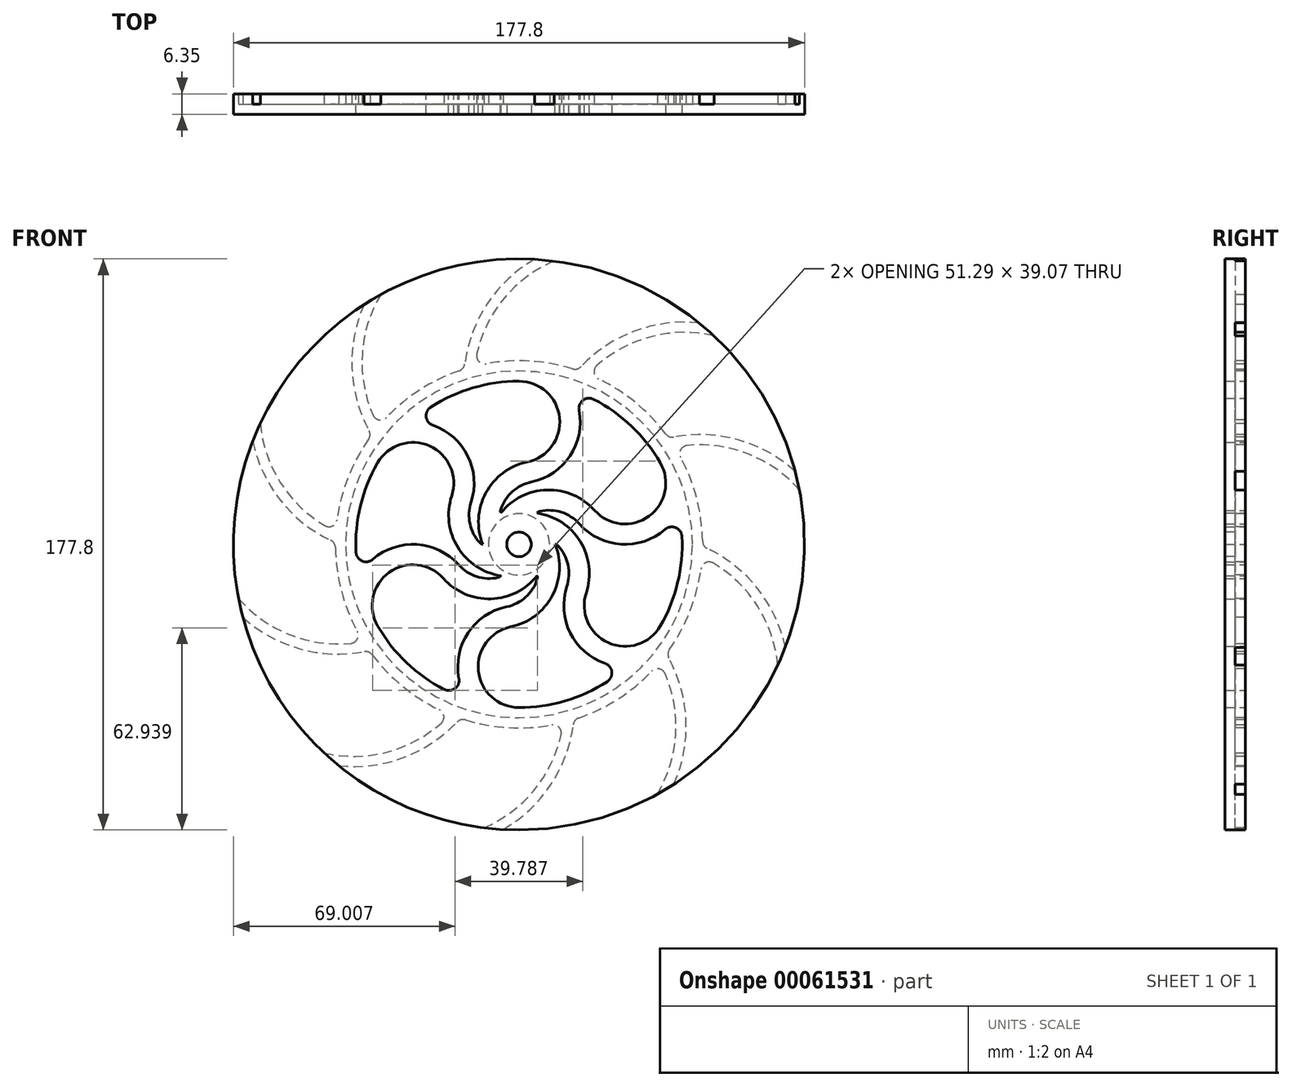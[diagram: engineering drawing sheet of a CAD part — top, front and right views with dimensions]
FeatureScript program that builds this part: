
annotation { "Feature Type Name" : "Feature", "Feature Type Description" : "" }
export const myFeature = defineFeature(function(context is Context, id is Id, definition is map)
    precondition{}
    {
        {
            var Q0;
            Q0=qCreatedBy(makeId("Front.planeOp"),FACE);
            var sketch = newSketch(context, id + "F0", { "sketchPlane" : qUnion([Q0])});
            skCircle(sketch, "E0", {"center": v(0, 0) * mm, "radius": 88.9 * mm});
            skSolve(sketch);
        }
        {
            var Q0;
            Q0=makeQuery(id+"F0.imprint","IMPRINT",FACE,{"disambiguationData":[TD([[makeQuery(id+"F0.imprint","IMPRINT",EDGE,{"derivedFrom":sQuery(id+"F0.wireOp",EDGE,"E0")}),1.0]])]});
            extrude(context, id + "F1", {"entities" : qUnion([Q0]), "depth" : 6.35 * mm});
        }
        {
            var Q0;
            Q0=makeQuery(id+"F1.opExtrude","CAP_FACE",FACE,{"disambiguationData":[OSD([sQuery(id+"F0.wireOp",EDGE,"E0")])],"isStart":false});
            var sketch = newSketch(context, id + "F2", { "sketchPlane" : qUnion([Q0])});
            skCircle(sketch, "E1", {"center": v(0, 0) * mm, "radius": 57.15 * mm});
            skCircle(sketch, "E2", {"center": v(0, 0) * mm, "radius": 53.98 * mm});
            skSolve(sketch);
        }
        {
            var Q0;
            Q0=qSketchRegion(id+"F2",true);
            extrude(context, id + "F3", {"entities" : qUnion([Q0]), "operationType" : NewBodyOperationType.ADD, "depth" : 41.27 * mm});
        }
        {
            var Q0;
            {var subQ0=sQuery(id+"F0.wireOp",EDGE,"E0");Q0=makeQuery(id+"F3.boolean.opBoolean","SPLIT",FACE,{"disambiguationData":[TD([makeQuery(id+"F1.opExtrude","SWEPT_FACE",FACE,{"disambiguationData":[OSD([subQ0])]})])],"derivedFrom":makeQuery(id+"F1.opExtrude","CAP_FACE",FACE,{"disambiguationData":[OSD([subQ0])],"isStart":false})});}
            var sketch = newSketch(context, id + "F4", { "sketchPlane" : qUnion([Q0])});
            skArc(sketch, "E3", {"start": v(80.54, -37.63) * mm, "mid": v(72.26, -16.34) * mm, "end": v(53.9, -2.7) * mm});
            skArc(sketch, "E4", {"start": v(82.9, -32.09) * mm, "mid": v(72.74, -11.92) * mm, "end": v(53.97, 0.64) * mm});
            skArc(sketch, "E5.0", {"start": v(53.9, -2.7) * mm, "mid": v(53.97, -1.03) * mm, "end": v(53.97, 0.64) * mm});
            skArc(sketch, "E6.0", {"start": v(80.54, -37.63) * mm, "mid": v(81.77, -34.88) * mm, "end": v(82.9, -32.09) * mm});
            skArc(sketch, "E7.1.0", {"start": v(87.28, 16.9) * mm, "mid": v(68.06, 29.26) * mm, "end": v(45.2, 29.5) * mm});
            skArc(sketch, "E7.1.1", {"start": v(85.93, 22.77) * mm, "mid": v(65.85, 33.1) * mm, "end": v(43.29, 32.24) * mm});
            skArc(sketch, "E7.1.2", {"start": v(87.28, 16.9) * mm, "mid": v(86.66, 19.84) * mm, "end": v(85.93, 22.77) * mm});
            skArc(sketch, "E7.1.3", {"start": v(45.2, 29.5) * mm, "mid": v(44.27, 30.88) * mm, "end": v(43.29, 32.24) * mm});
            skArc(sketch, "E7.2.0", {"start": v(60.68, 64.97) * mm, "mid": v(37.86, 63.67) * mm, "end": v(19.24, 50.43) * mm});
            skArc(sketch, "E7.2.1", {"start": v(56.14, 68.93) * mm, "mid": v(33.82, 65.5) * mm, "end": v(16.07, 51.53) * mm});
            skArc(sketch, "E7.2.2", {"start": v(60.68, 64.97) * mm, "mid": v(58.44, 66.99) * mm, "end": v(56.14, 68.93) * mm});
            skArc(sketch, "E7.2.3", {"start": v(19.24, 50.43) * mm, "mid": v(17.66, 51) * mm, "end": v(16.07, 51.53) * mm});
            skArc(sketch, "E7.3.0", {"start": v(10.9, 88.23) * mm, "mid": v(-6.8, 73.77) * mm, "end": v(-14.08, 52.1) * mm});
            skArc(sketch, "E7.3.1", {"start": v(4.9, 88.76) * mm, "mid": v(-11.14, 72.86) * mm, "end": v(-17.29, 51.13) * mm});
            skArc(sketch, "E7.3.2", {"start": v(10.9, 88.23) * mm, "mid": v(7.9, 88.55) * mm, "end": v(4.9, 88.76) * mm});
            skArc(sketch, "E7.3.3", {"start": v(-14.08, 52.1) * mm, "mid": v(-15.7, 51.64) * mm, "end": v(-17.29, 51.13) * mm});
            skArc(sketch, "E7.4.0", {"start": v(-43.04, 77.79) * mm, "mid": v(-48.85, 55.69) * mm, "end": v(-42.02, 33.88) * mm});
            skArc(sketch, "E7.4.1", {"start": v(-48.21, 74.7) * mm, "mid": v(-51.84, 52.4) * mm, "end": v(-44.04, 31.2) * mm});
            skArc(sketch, "E7.4.2", {"start": v(-43.04, 77.79) * mm, "mid": v(-45.65, 76.28) * mm, "end": v(-48.21, 74.7) * mm});
            skArc(sketch, "E7.4.3", {"start": v(-42.02, 33.88) * mm, "mid": v(-43.05, 32.56) * mm, "end": v(-44.04, 31.2) * mm});
            skArc(sketch, "E7.5.0", {"start": v(-80.54, 37.63) * mm, "mid": v(-72.26, 16.34) * mm, "end": v(-53.9, 2.7) * mm});
            skArc(sketch, "E7.5.1", {"start": v(-82.9, 32.09) * mm, "mid": v(-72.74, 11.92) * mm, "end": v(-53.97, -0.64) * mm});
            skArc(sketch, "E7.5.2", {"start": v(-80.54, 37.63) * mm, "mid": v(-81.77, 34.88) * mm, "end": v(-82.9, 32.09) * mm});
            skArc(sketch, "E7.5.3", {"start": v(-53.9, 2.7) * mm, "mid": v(-53.97, 1.03) * mm, "end": v(-53.97, -0.64) * mm});
            skArc(sketch, "E7.6.0", {"start": v(-87.28, -16.9) * mm, "mid": v(-68.06, -29.26) * mm, "end": v(-45.2, -29.5) * mm});
            skArc(sketch, "E7.6.1", {"start": v(-85.93, -22.77) * mm, "mid": v(-65.85, -33.1) * mm, "end": v(-43.29, -32.24) * mm});
            skArc(sketch, "E7.6.2", {"start": v(-87.28, -16.9) * mm, "mid": v(-86.66, -19.84) * mm, "end": v(-85.93, -22.77) * mm});
            skArc(sketch, "E7.6.3", {"start": v(-45.2, -29.5) * mm, "mid": v(-44.27, -30.88) * mm, "end": v(-43.29, -32.24) * mm});
            skArc(sketch, "E7.7.0", {"start": v(-60.68, -64.97) * mm, "mid": v(-37.86, -63.67) * mm, "end": v(-19.24, -50.43) * mm});
            skArc(sketch, "E7.7.1", {"start": v(-56.14, -68.93) * mm, "mid": v(-33.82, -65.5) * mm, "end": v(-16.07, -51.53) * mm});
            skArc(sketch, "E7.7.2", {"start": v(-60.68, -64.97) * mm, "mid": v(-58.44, -66.99) * mm, "end": v(-56.14, -68.93) * mm});
            skArc(sketch, "E7.7.3", {"start": v(-19.24, -50.43) * mm, "mid": v(-17.66, -51) * mm, "end": v(-16.07, -51.53) * mm});
            skArc(sketch, "E7.8.0", {"start": v(-10.9, -88.23) * mm, "mid": v(6.8, -73.77) * mm, "end": v(14.08, -52.1) * mm});
            skArc(sketch, "E7.8.1", {"start": v(-4.9, -88.76) * mm, "mid": v(11.14, -72.86) * mm, "end": v(17.29, -51.13) * mm});
            skArc(sketch, "E7.8.2", {"start": v(-10.9, -88.23) * mm, "mid": v(-7.9, -88.55) * mm, "end": v(-4.9, -88.76) * mm});
            skArc(sketch, "E7.8.3", {"start": v(14.08, -52.1) * mm, "mid": v(15.7, -51.64) * mm, "end": v(17.29, -51.13) * mm});
            skArc(sketch, "E7.9.0", {"start": v(43.04, -77.79) * mm, "mid": v(48.85, -55.69) * mm, "end": v(42.02, -33.88) * mm});
            skArc(sketch, "E7.9.1", {"start": v(48.21, -74.7) * mm, "mid": v(51.84, -52.4) * mm, "end": v(44.04, -31.2) * mm});
            skArc(sketch, "E7.9.2", {"start": v(43.04, -77.79) * mm, "mid": v(45.65, -76.28) * mm, "end": v(48.21, -74.7) * mm});
            skArc(sketch, "E7.9.3", {"start": v(42.02, -33.88) * mm, "mid": v(43.05, -32.56) * mm, "end": v(44.04, -31.2) * mm});
            skSolve(sketch);
        }
        {
            var Q0;
            Q0=qSketchRegion(id+"F4",true);
            var Q1;
            Q1=makeQuery(id+"F3.opExtrude","CAP_FACE",FACE,{"disambiguationData":[OSD([sQuery(id+"F2.wireOp",EDGE,"E1"),sQuery(id+"F2.wireOp",EDGE,"E2")])],"isStart":false});
            extrude(context, id + "F5", {"entities" : qUnion([Q0]), "operationType" : NewBodyOperationType.ADD, "endBound" : BoundingType.UP_TO_SURFACE, "endBoundEntityFace" : qUnion([Q1]), "depth" : 25.4 * mm});
        }
        {
            var Q0;
            Q0=makeQuery(id+"F3.boolean.opBoolean","SPLIT",FACE,{"disambiguationData":[TD([makeQuery(id+"F3.opExtrude","SWEPT_FACE",FACE,{"disambiguationData":[OSD([sQuery(id+"F2.wireOp",EDGE,"E2")])]})])],"derivedFrom":makeQuery(id+"F1.opExtrude","CAP_FACE",FACE,{"disambiguationData":[OSD([sQuery(id+"F0.wireOp",EDGE,"E0")])],"isStart":false})});
            var sketch = newSketch(context, id + "F6", { "sketchPlane" : qUnion([Q0])});
            skCircle(sketch, "E8", {"center": v(0, 0) * mm, "radius": 3.81 * mm});
            skCircle(sketch, "E9", {"center": v(0, 0) * mm, "radius": 9.53 * mm});
            skSolve(sketch);
        }
        {
            var Q0;
            Q0=qSketchRegion(id+"F6",true);
            var Q1;
            {var subQ0=sQuery(id+"F2.wireOp",EDGE,"E2");var subQ1=sQuery(id+"F2.wireOp",EDGE,"E1");Q1=makeQuery(id+"F5.boolean.opBoolean","MERGE",FACE,{"derivedFrom":[makeQuery(id+"F3.opExtrude","CAP_FACE",FACE,{"disambiguationData":[OSD([subQ1,subQ0])],"isStart":false}),makeQuery(id+"F5.opExtrude","CAP_FACE",FACE,{"disambiguationData":[OSD([subQ1,subQ0]),ownerDisambiguation([makeQuery(id+"F5.opExtrude","SWEPT_BODY",BODY,{"disambiguationData":[OSD([sQuery(id+"F4.wireOp",EDGE,"E3"),sQuery(id+"F4.wireOp",EDGE,"E4"),sQuery(id+"F4.wireOp",EDGE,"E5.0"),sQuery(id+"F4.wireOp",EDGE,"E6.0")])]})])],"isStart":false}),makeQuery(id+"F5.opExtrude","CAP_FACE",FACE,{"disambiguationData":[OSD([subQ1,subQ0]),ownerDisambiguation([makeQuery(id+"F5.opExtrude","SWEPT_BODY",BODY,{"disambiguationData":[OSD([sQuery(id+"F4.wireOp",EDGE,"E7.1.0"),sQuery(id+"F4.wireOp",EDGE,"E7.1.1"),sQuery(id+"F4.wireOp",EDGE,"E7.1.2"),sQuery(id+"F4.wireOp",EDGE,"E7.1.3")])]})])],"isStart":false}),makeQuery(id+"F5.opExtrude","CAP_FACE",FACE,{"disambiguationData":[OSD([subQ1,subQ0]),ownerDisambiguation([makeQuery(id+"F5.opExtrude","SWEPT_BODY",BODY,{"disambiguationData":[OSD([sQuery(id+"F4.wireOp",EDGE,"E7.2.0"),sQuery(id+"F4.wireOp",EDGE,"E7.2.1"),sQuery(id+"F4.wireOp",EDGE,"E7.2.2"),sQuery(id+"F4.wireOp",EDGE,"E7.2.3")])]})])],"isStart":false}),makeQuery(id+"F5.opExtrude","CAP_FACE",FACE,{"disambiguationData":[OSD([subQ1,subQ0]),ownerDisambiguation([makeQuery(id+"F5.opExtrude","SWEPT_BODY",BODY,{"disambiguationData":[OSD([sQuery(id+"F4.wireOp",EDGE,"E7.3.0"),sQuery(id+"F4.wireOp",EDGE,"E7.3.1"),sQuery(id+"F4.wireOp",EDGE,"E7.3.2"),sQuery(id+"F4.wireOp",EDGE,"E7.3.3")])]})])],"isStart":false}),makeQuery(id+"F5.opExtrude","CAP_FACE",FACE,{"disambiguationData":[OSD([subQ1,subQ0]),ownerDisambiguation([makeQuery(id+"F5.opExtrude","SWEPT_BODY",BODY,{"disambiguationData":[OSD([sQuery(id+"F4.wireOp",EDGE,"E7.4.0"),sQuery(id+"F4.wireOp",EDGE,"E7.4.1"),sQuery(id+"F4.wireOp",EDGE,"E7.4.2"),sQuery(id+"F4.wireOp",EDGE,"E7.4.3")])]})])],"isStart":false}),makeQuery(id+"F5.opExtrude","CAP_FACE",FACE,{"disambiguationData":[OSD([subQ1,subQ0]),ownerDisambiguation([makeQuery(id+"F5.opExtrude","SWEPT_BODY",BODY,{"disambiguationData":[OSD([sQuery(id+"F4.wireOp",EDGE,"E7.5.0"),sQuery(id+"F4.wireOp",EDGE,"E7.5.1"),sQuery(id+"F4.wireOp",EDGE,"E7.5.2"),sQuery(id+"F4.wireOp",EDGE,"E7.5.3")])]})])],"isStart":false}),makeQuery(id+"F5.opExtrude","CAP_FACE",FACE,{"disambiguationData":[OSD([subQ1,subQ0]),ownerDisambiguation([makeQuery(id+"F5.opExtrude","SWEPT_BODY",BODY,{"disambiguationData":[OSD([sQuery(id+"F4.wireOp",EDGE,"E7.6.0"),sQuery(id+"F4.wireOp",EDGE,"E7.6.1"),sQuery(id+"F4.wireOp",EDGE,"E7.6.2"),sQuery(id+"F4.wireOp",EDGE,"E7.6.3")])]})])],"isStart":false}),makeQuery(id+"F5.opExtrude","CAP_FACE",FACE,{"disambiguationData":[OSD([subQ1,subQ0]),ownerDisambiguation([makeQuery(id+"F5.opExtrude","SWEPT_BODY",BODY,{"disambiguationData":[OSD([sQuery(id+"F4.wireOp",EDGE,"E7.7.0"),sQuery(id+"F4.wireOp",EDGE,"E7.7.1"),sQuery(id+"F4.wireOp",EDGE,"E7.7.2"),sQuery(id+"F4.wireOp",EDGE,"E7.7.3")])]})])],"isStart":false}),makeQuery(id+"F5.opExtrude","CAP_FACE",FACE,{"disambiguationData":[OSD([subQ1,subQ0]),ownerDisambiguation([makeQuery(id+"F5.opExtrude","SWEPT_BODY",BODY,{"disambiguationData":[OSD([sQuery(id+"F4.wireOp",EDGE,"E7.8.0"),sQuery(id+"F4.wireOp",EDGE,"E7.8.1"),sQuery(id+"F4.wireOp",EDGE,"E7.8.2"),sQuery(id+"F4.wireOp",EDGE,"E7.8.3")])]})])],"isStart":false}),makeQuery(id+"F5.opExtrude","CAP_FACE",FACE,{"disambiguationData":[OSD([subQ1,subQ0]),ownerDisambiguation([makeQuery(id+"F5.opExtrude","SWEPT_BODY",BODY,{"disambiguationData":[OSD([sQuery(id+"F4.wireOp",EDGE,"E7.9.0"),sQuery(id+"F4.wireOp",EDGE,"E7.9.1"),sQuery(id+"F4.wireOp",EDGE,"E7.9.2"),sQuery(id+"F4.wireOp",EDGE,"E7.9.3")])]})])],"isStart":false})]});}
            extrude(context, id + "F7", {"entities" : qUnion([Q0]), "operationType" : NewBodyOperationType.ADD, "endBound" : BoundingType.UP_TO_SURFACE, "endBoundEntityFace" : qUnion([Q1]), "depth" : 25.4 * mm});
        }
        {
            var Q0;
            {var subQ0=makeQuery(id+"F3.opExtrude","SWEPT_FACE",FACE,{"disambiguationData":[OSD([sQuery(id+"F2.wireOp",EDGE,"E2")])]});Q0=makeQuery(id+"F7.boolean.opBoolean","SPLIT",FACE,{"disambiguationData":[TD([subQ0])],"derivedFrom":makeQuery(id+"F3.boolean.opBoolean","SPLIT",FACE,{"disambiguationData":[TD([subQ0])],"derivedFrom":makeQuery(id+"F1.opExtrude","CAP_FACE",FACE,{"disambiguationData":[OSD([sQuery(id+"F0.wireOp",EDGE,"E0")])],"isStart":false})})});}
            var sketch = newSketch(context, id + "F8", { "sketchPlane" : qUnion([Q0])});
            skCircle(sketch, "E10.0", {"center": v(0, 0) * mm, "radius": 3.81 * mm});
            skArc(sketch, "E11", {"start": v(0, 50.8) * mm, "mid": v(-14.31, 48.74) * mm, "end": v(-27.47, 42.73) * mm, "construction": true});
            skArc(sketch, "E12", {"start": v(3.87, 19.45) * mm, "mid": v(-2.1, 16.41) * mm, "end": v(-5.68, 10.77) * mm});
            skArc(sketch, "E13", {"start": v(2.58, 25.66) * mm, "mid": v(-10.33, 16.04) * mm, "end": v(-11.26, -0.03) * mm});
            skArc(sketch, "E14", {"start": v(2.58, 25.66) * mm, "mid": v(12.63, 39.4) * mm, "end": v(0, 50.8) * mm});
            skArc(sketch, "E15", {"start": v(3.87, 19.45) * mm, "mid": v(15.86, 27.54) * mm, "end": v(18.7, 41.73) * mm});
            skPoint(sketch, "E16.visualSharp", {"position": v(16.18, 48.15) * mm});
            skArc(sketch, "E16.filletArc", {"start": v(23.27, 45.16) * mm, "mid": v(19.91, 44.87) * mm, "end": v(18.7, 41.73) * mm});
            skPoint(sketch, "E17.visualSharp", {"position": v(-6.25, 7.19) * mm});
            skArc(sketch, "E17.filletArc", {"start": v(-5.68, 10.77) * mm, "mid": v(-5.75, 10.25) * mm, "end": v(-5.65, 9.73) * mm});
            skPoint(sketch, "E18.1.1", {"position": v(-33.61, 38.1) * mm});
            skArc(sketch, "E18.1.2", {"start": v(-14.9, 13.07) * mm, "mid": v(-15.26, 6.4) * mm, "end": v(-12.17, 0.46) * mm});
            skArc(sketch, "E18.1.3", {"start": v(-20.94, 15.07) * mm, "mid": v(-27.8, 30.64) * mm, "end": v(-44, 25.4) * mm});
            skArc(sketch, "E18.1.4", {"start": v(-20.94, 15.07) * mm, "mid": v(-19.06, -0.92) * mm, "end": v(-5.6, -9.76) * mm});
            skPoint(sketch, "E18.1.5", {"position": v(-9.35, -1.82) * mm});
            skArc(sketch, "E18.1.6", {"start": v(-14.9, 13.07) * mm, "mid": v(-15.92, 27.5) * mm, "end": v(-26.79, 37.06) * mm});
            skArc(sketch, "E18.1.7", {"start": v(-27.47, 42.73) * mm, "mid": v(-28.9, 39.68) * mm, "end": v(-26.79, 37.06) * mm});
            skArc(sketch, "E18.1.8", {"start": v(-12.17, 0.46) * mm, "mid": v(-11.75, 0.14) * mm, "end": v(-11.26, -0.03) * mm});
            skPoint(sketch, "E18.2.1", {"position": v(-49.8, -10.06) * mm});
            skArc(sketch, "E18.2.2", {"start": v(-18.78, -6.37) * mm, "mid": v(-13.17, -10.02) * mm, "end": v(-6.49, -10.3) * mm});
            skArc(sketch, "E18.2.3", {"start": v(-23.52, -10.6) * mm, "mid": v(-40.43, -8.76) * mm, "end": v(-44, -25.4) * mm});
            skArc(sketch, "E18.2.4", {"start": v(-23.52, -10.6) * mm, "mid": v(-8.73, -16.96) * mm, "end": v(5.65, -9.73) * mm});
            skPoint(sketch, "E18.2.5", {"position": v(-3.1, -9) * mm});
            skArc(sketch, "E18.2.6", {"start": v(-18.78, -6.37) * mm, "mid": v(-31.78, -0.04) * mm, "end": v(-45.49, -4.67) * mm});
            skArc(sketch, "E18.2.7", {"start": v(-50.74, -2.42) * mm, "mid": v(-48.82, -5.2) * mm, "end": v(-45.49, -4.67) * mm});
            skArc(sketch, "E18.2.8", {"start": v(-6.49, -10.3) * mm, "mid": v(-6, -10.1) * mm, "end": v(-5.6, -9.76) * mm});
            skPoint(sketch, "E18.3.1", {"position": v(-16.18, -48.15) * mm});
            skArc(sketch, "E18.3.2", {"start": v(-3.87, -19.45) * mm, "mid": v(2.1, -16.41) * mm, "end": v(5.68, -10.77) * mm});
            skArc(sketch, "E18.3.3", {"start": v(-2.58, -25.66) * mm, "mid": v(-12.63, -39.4) * mm, "end": v(0, -50.8) * mm});
            skArc(sketch, "E18.3.4", {"start": v(-2.58, -25.66) * mm, "mid": v(10.33, -16.04) * mm, "end": v(11.26, 0.03) * mm});
            skPoint(sketch, "E18.3.5", {"position": v(6.25, -7.19) * mm});
            skArc(sketch, "E18.3.6", {"start": v(-3.87, -19.45) * mm, "mid": v(-15.86, -27.54) * mm, "end": v(-18.7, -41.73) * mm});
            skArc(sketch, "E18.3.7", {"start": v(-23.27, -45.16) * mm, "mid": v(-19.91, -44.87) * mm, "end": v(-18.7, -41.73) * mm});
            skArc(sketch, "E18.3.8", {"start": v(5.68, -10.77) * mm, "mid": v(5.75, -10.25) * mm, "end": v(5.65, -9.73) * mm});
            skPoint(sketch, "E18.4.1", {"position": v(33.61, -38.1) * mm});
            skArc(sketch, "E18.4.2", {"start": v(14.9, -13.07) * mm, "mid": v(15.26, -6.4) * mm, "end": v(12.17, -0.46) * mm});
            skArc(sketch, "E18.4.3", {"start": v(20.94, -15.07) * mm, "mid": v(27.8, -30.64) * mm, "end": v(44, -25.4) * mm});
            skArc(sketch, "E18.4.4", {"start": v(20.94, -15.07) * mm, "mid": v(19.06, 0.92) * mm, "end": v(5.6, 9.76) * mm});
            skPoint(sketch, "E18.4.5", {"position": v(9.35, 1.82) * mm});
            skArc(sketch, "E18.4.6", {"start": v(14.9, -13.07) * mm, "mid": v(15.92, -27.5) * mm, "end": v(26.79, -37.06) * mm});
            skArc(sketch, "E18.4.7", {"start": v(27.47, -42.73) * mm, "mid": v(28.9, -39.68) * mm, "end": v(26.79, -37.06) * mm});
            skArc(sketch, "E18.4.8", {"start": v(12.17, -0.46) * mm, "mid": v(11.75, -0.14) * mm, "end": v(11.26, 0.03) * mm});
            skPoint(sketch, "E18.5.1", {"position": v(49.8, 10.06) * mm});
            skArc(sketch, "E18.5.2", {"start": v(18.78, 6.37) * mm, "mid": v(13.17, 10.02) * mm, "end": v(6.49, 10.3) * mm});
            skArc(sketch, "E18.5.3", {"start": v(23.52, 10.6) * mm, "mid": v(40.43, 8.76) * mm, "end": v(44, 25.4) * mm});
            skArc(sketch, "E18.5.4", {"start": v(23.52, 10.6) * mm, "mid": v(8.73, 16.96) * mm, "end": v(-5.65, 9.73) * mm});
            skPoint(sketch, "E18.5.5", {"position": v(3.1, 9) * mm});
            skArc(sketch, "E18.5.6", {"start": v(18.78, 6.37) * mm, "mid": v(31.78, 0.04) * mm, "end": v(45.49, 4.67) * mm});
            skArc(sketch, "E18.5.7", {"start": v(50.74, 2.42) * mm, "mid": v(48.82, 5.2) * mm, "end": v(45.49, 4.67) * mm});
            skArc(sketch, "E18.5.8", {"start": v(6.49, 10.3) * mm, "mid": v(6, 10.1) * mm, "end": v(5.6, 9.76) * mm});
            skArc(sketch, "E19", {"start": v(44, 25.4) * mm, "mid": v(35.05, 36.77) * mm, "end": v(23.27, 45.16) * mm});
            skArc(sketch, "E20.trimOffspring", {"start": v(44, -25.4) * mm, "mid": v(49.37, -11.97) * mm, "end": v(50.74, 2.42) * mm});
            skArc(sketch, "E21.trimOffspring", {"start": v(0, 50.8) * mm, "mid": v(-14.31, 48.74) * mm, "end": v(-27.47, 42.73) * mm});
            skArc(sketch, "E22.trimOffspring", {"start": v(44, 25.4) * mm, "mid": v(35.05, 36.77) * mm, "end": v(23.27, 45.16) * mm, "construction": true});
            skArc(sketch, "E23.trimOffspring", {"start": v(44, -25.4) * mm, "mid": v(49.37, -11.97) * mm, "end": v(50.74, 2.42) * mm, "construction": true});
            skArc(sketch, "E24.trimOffspring", {"start": v(0, -50.8) * mm, "mid": v(14.31, -48.74) * mm, "end": v(27.47, -42.73) * mm});
            skArc(sketch, "E25.trimOffspring", {"start": v(0, -50.8) * mm, "mid": v(14.31, -48.74) * mm, "end": v(27.47, -42.73) * mm, "construction": true});
            skArc(sketch, "E26.trimOffspring", {"start": v(-44, 25.4) * mm, "mid": v(-49.37, 11.97) * mm, "end": v(-50.74, -2.42) * mm});
            skArc(sketch, "E27.trimOffspring", {"start": v(-44, -25.4) * mm, "mid": v(-35.05, -36.77) * mm, "end": v(-23.27, -45.16) * mm});
            skArc(sketch, "E28.trimOffspring", {"start": v(-44, -25.4) * mm, "mid": v(-35.05, -36.77) * mm, "end": v(-23.27, -45.16) * mm, "construction": true});
            skArc(sketch, "E29.trimOffspring", {"start": v(-44, 25.4) * mm, "mid": v(-49.37, 11.97) * mm, "end": v(-50.74, -2.42) * mm, "construction": true});
            skPoint(sketch, "E30.orphan", {"position": v(9.43, -1.32) * mm});
            skPoint(sketch, "E31.orphan", {"position": v(5.86, 7.5) * mm});
            skPoint(sketch, "E32.orphan", {"position": v(-3.57, 8.83) * mm});
            skPoint(sketch, "E33.orphan", {"position": v(-9.43, 1.32) * mm});
            skPoint(sketch, "E34.orphan", {"position": v(-5.86, -7.5) * mm});
            skPoint(sketch, "E35.orphan", {"position": v(3.57, -8.83) * mm});
            skSolve(sketch);
        }
        {
            var Q0;
            Q0=qSketchRegion(id+"F8",true);
            extrude(context, id + "F9", {"entities" : qUnion([Q0]), "operationType" : NewBodyOperationType.REMOVE, "oppositeDirection" : true, "depth" : 25.4 * mm});
        }
        {
            var Q0;
            Q0=makeQuery(id+"F5.boolean.opBoolean","INTERSECT",EDGE,{"derivedFrom":[makeQuery(id+"F3.opExtrude","SWEPT_FACE",FACE,{"disambiguationData":[OSD([sQuery(id+"F2.wireOp",EDGE,"E1")])]}),makeQuery(id+"F5.opExtrude","SWEPT_FACE",FACE,{"disambiguationData":[OSD([sQuery(id+"F4.wireOp",EDGE,"E7.1.0")])]})]});
            var Q1;
            Q1=makeQuery(id+"F5.boolean.opBoolean","INTERSECT",EDGE,{"derivedFrom":[makeQuery(id+"F3.opExtrude","SWEPT_FACE",FACE,{"disambiguationData":[OSD([sQuery(id+"F2.wireOp",EDGE,"E1")])]}),makeQuery(id+"F5.opExtrude","SWEPT_FACE",FACE,{"disambiguationData":[OSD([sQuery(id+"F4.wireOp",EDGE,"E4")])]})]});
            var Q2;
            Q2=makeQuery(id+"F5.boolean.opBoolean","INTERSECT",EDGE,{"derivedFrom":[makeQuery(id+"F3.opExtrude","SWEPT_FACE",FACE,{"disambiguationData":[OSD([sQuery(id+"F2.wireOp",EDGE,"E1")])]}),makeQuery(id+"F5.opExtrude","SWEPT_FACE",FACE,{"disambiguationData":[OSD([sQuery(id+"F4.wireOp",EDGE,"E3")])]})]});
            var Q3;
            Q3=makeQuery(id+"F5.boolean.opBoolean","INTERSECT",EDGE,{"derivedFrom":[makeQuery(id+"F3.opExtrude","SWEPT_FACE",FACE,{"disambiguationData":[OSD([sQuery(id+"F2.wireOp",EDGE,"E1")])]}),makeQuery(id+"F5.opExtrude","SWEPT_FACE",FACE,{"disambiguationData":[OSD([sQuery(id+"F4.wireOp",EDGE,"E7.9.1")])]})]});
            var Q4;
            Q4=makeQuery(id+"F5.boolean.opBoolean","INTERSECT",EDGE,{"derivedFrom":[makeQuery(id+"F3.opExtrude","SWEPT_FACE",FACE,{"disambiguationData":[OSD([sQuery(id+"F2.wireOp",EDGE,"E1")])]}),makeQuery(id+"F5.opExtrude","SWEPT_FACE",FACE,{"disambiguationData":[OSD([sQuery(id+"F4.wireOp",EDGE,"E7.9.0")])]})]});
            var Q5;
            Q5=makeQuery(id+"F5.boolean.opBoolean","INTERSECT",EDGE,{"derivedFrom":[makeQuery(id+"F3.opExtrude","SWEPT_FACE",FACE,{"disambiguationData":[OSD([sQuery(id+"F2.wireOp",EDGE,"E1")])]}),makeQuery(id+"F5.opExtrude","SWEPT_FACE",FACE,{"disambiguationData":[OSD([sQuery(id+"F4.wireOp",EDGE,"E7.8.1")])]})]});
            var Q6;
            Q6=makeQuery(id+"F5.boolean.opBoolean","INTERSECT",EDGE,{"derivedFrom":[makeQuery(id+"F3.opExtrude","SWEPT_FACE",FACE,{"disambiguationData":[OSD([sQuery(id+"F2.wireOp",EDGE,"E1")])]}),makeQuery(id+"F5.opExtrude","SWEPT_FACE",FACE,{"disambiguationData":[OSD([sQuery(id+"F4.wireOp",EDGE,"E7.8.0")])]})]});
            var Q7;
            Q7=makeQuery(id+"F5.boolean.opBoolean","INTERSECT",EDGE,{"derivedFrom":[makeQuery(id+"F3.opExtrude","SWEPT_FACE",FACE,{"disambiguationData":[OSD([sQuery(id+"F2.wireOp",EDGE,"E1")])]}),makeQuery(id+"F5.opExtrude","SWEPT_FACE",FACE,{"disambiguationData":[OSD([sQuery(id+"F4.wireOp",EDGE,"E7.7.1")])]})]});
            var Q8;
            Q8=makeQuery(id+"F5.boolean.opBoolean","INTERSECT",EDGE,{"derivedFrom":[makeQuery(id+"F3.opExtrude","SWEPT_FACE",FACE,{"disambiguationData":[OSD([sQuery(id+"F2.wireOp",EDGE,"E1")])]}),makeQuery(id+"F5.opExtrude","SWEPT_FACE",FACE,{"disambiguationData":[OSD([sQuery(id+"F4.wireOp",EDGE,"E7.6.1")])]})]});
            var Q9;
            Q9=makeQuery(id+"F5.boolean.opBoolean","INTERSECT",EDGE,{"derivedFrom":[makeQuery(id+"F3.opExtrude","SWEPT_FACE",FACE,{"disambiguationData":[OSD([sQuery(id+"F2.wireOp",EDGE,"E1")])]}),makeQuery(id+"F5.opExtrude","SWEPT_FACE",FACE,{"disambiguationData":[OSD([sQuery(id+"F4.wireOp",EDGE,"E7.7.0")])]})]});
            var Q10;
            Q10=makeQuery(id+"F5.boolean.opBoolean","INTERSECT",EDGE,{"derivedFrom":[makeQuery(id+"F3.opExtrude","SWEPT_FACE",FACE,{"disambiguationData":[OSD([sQuery(id+"F2.wireOp",EDGE,"E1")])]}),makeQuery(id+"F5.opExtrude","SWEPT_FACE",FACE,{"disambiguationData":[OSD([sQuery(id+"F4.wireOp",EDGE,"E7.6.0")])]})]});
            var Q11;
            Q11=makeQuery(id+"F5.boolean.opBoolean","INTERSECT",EDGE,{"derivedFrom":[makeQuery(id+"F3.opExtrude","SWEPT_FACE",FACE,{"disambiguationData":[OSD([sQuery(id+"F2.wireOp",EDGE,"E1")])]}),makeQuery(id+"F5.opExtrude","SWEPT_FACE",FACE,{"disambiguationData":[OSD([sQuery(id+"F4.wireOp",EDGE,"E7.5.0")])]})]});
            var Q12;
            Q12=makeQuery(id+"F5.boolean.opBoolean","INTERSECT",EDGE,{"derivedFrom":[makeQuery(id+"F3.opExtrude","SWEPT_FACE",FACE,{"disambiguationData":[OSD([sQuery(id+"F2.wireOp",EDGE,"E1")])]}),makeQuery(id+"F5.opExtrude","SWEPT_FACE",FACE,{"disambiguationData":[OSD([sQuery(id+"F4.wireOp",EDGE,"E7.4.1")])]})]});
            var Q13;
            Q13=makeQuery(id+"F5.boolean.opBoolean","INTERSECT",EDGE,{"derivedFrom":[makeQuery(id+"F3.opExtrude","SWEPT_FACE",FACE,{"disambiguationData":[OSD([sQuery(id+"F2.wireOp",EDGE,"E1")])]}),makeQuery(id+"F5.opExtrude","SWEPT_FACE",FACE,{"disambiguationData":[OSD([sQuery(id+"F4.wireOp",EDGE,"E7.5.1")])]})]});
            var Q14;
            Q14=makeQuery(id+"F5.boolean.opBoolean","INTERSECT",EDGE,{"derivedFrom":[makeQuery(id+"F3.opExtrude","SWEPT_FACE",FACE,{"disambiguationData":[OSD([sQuery(id+"F2.wireOp",EDGE,"E1")])]}),makeQuery(id+"F5.opExtrude","SWEPT_FACE",FACE,{"disambiguationData":[OSD([sQuery(id+"F4.wireOp",EDGE,"E7.4.0")])]})]});
            var Q15;
            Q15=makeQuery(id+"F5.boolean.opBoolean","INTERSECT",EDGE,{"derivedFrom":[makeQuery(id+"F3.opExtrude","SWEPT_FACE",FACE,{"disambiguationData":[OSD([sQuery(id+"F2.wireOp",EDGE,"E1")])]}),makeQuery(id+"F5.opExtrude","SWEPT_FACE",FACE,{"disambiguationData":[OSD([sQuery(id+"F4.wireOp",EDGE,"E7.3.1")])]})]});
            var Q16;
            Q16=makeQuery(id+"F5.boolean.opBoolean","INTERSECT",EDGE,{"derivedFrom":[makeQuery(id+"F3.opExtrude","SWEPT_FACE",FACE,{"disambiguationData":[OSD([sQuery(id+"F2.wireOp",EDGE,"E1")])]}),makeQuery(id+"F5.opExtrude","SWEPT_FACE",FACE,{"disambiguationData":[OSD([sQuery(id+"F4.wireOp",EDGE,"E7.3.0")])]})]});
            var Q17;
            Q17=makeQuery(id+"F5.boolean.opBoolean","INTERSECT",EDGE,{"derivedFrom":[makeQuery(id+"F3.opExtrude","SWEPT_FACE",FACE,{"disambiguationData":[OSD([sQuery(id+"F2.wireOp",EDGE,"E1")])]}),makeQuery(id+"F5.opExtrude","SWEPT_FACE",FACE,{"disambiguationData":[OSD([sQuery(id+"F4.wireOp",EDGE,"E7.2.1")])]})]});
            var Q18;
            Q18=makeQuery(id+"F5.boolean.opBoolean","INTERSECT",EDGE,{"derivedFrom":[makeQuery(id+"F3.opExtrude","SWEPT_FACE",FACE,{"disambiguationData":[OSD([sQuery(id+"F2.wireOp",EDGE,"E1")])]}),makeQuery(id+"F5.opExtrude","SWEPT_FACE",FACE,{"disambiguationData":[OSD([sQuery(id+"F4.wireOp",EDGE,"E7.2.0")])]})]});
            var Q19;
            Q19=makeQuery(id+"F5.boolean.opBoolean","INTERSECT",EDGE,{"derivedFrom":[makeQuery(id+"F3.opExtrude","SWEPT_FACE",FACE,{"disambiguationData":[OSD([sQuery(id+"F2.wireOp",EDGE,"E1")])]}),makeQuery(id+"F5.opExtrude","SWEPT_FACE",FACE,{"disambiguationData":[OSD([sQuery(id+"F4.wireOp",EDGE,"E7.1.1")])]})]});
            fillet(context, id + "F10", {"entities" : qUnion([Q0, Q1, Q2, Q3, Q4, Q5, Q6, Q7, Q8, Q9, Q10, Q11, Q12, Q13, Q14, Q15, Q16, Q17, Q18, Q19]), "radius" : 2.54 * mm, "tangentPropagation" : true, "allowEdgeOverflow" : false});
        }
        {
            var Q0;
            {var subQ0=makeQuery(id+"F3.opExtrude","SWEPT_FACE",FACE,{"disambiguationData":[OSD([sQuery(id+"F2.wireOp",EDGE,"E2")])]});Q0=makeQuery(id+"F7.boolean.opBoolean","SPLIT",FACE,{"disambiguationData":[TD([subQ0])],"derivedFrom":makeQuery(id+"F3.boolean.opBoolean","SPLIT",FACE,{"disambiguationData":[TD([subQ0])],"derivedFrom":makeQuery(id+"F1.opExtrude","CAP_FACE",FACE,{"disambiguationData":[OSD([sQuery(id+"F0.wireOp",EDGE,"E0")])],"isStart":false})})});}
            var sketch = newSketch(context, id + "F11", { "sketchPlane" : qUnion([Q0])});
            skArc(sketch, "E36.0.0", {"start": v(-4.9, -88.76) * mm, "mid": v(9.8, -74.98) * mm, "end": v(16.91, -56.1) * mm});
            skArc(sketch, "E36.0.1", {"start": v(16.91, -56.1) * mm, "mid": v(17.47, -54.83) * mm, "end": v(18.6, -54.04) * mm});
            skArc(sketch, "E36.0.2", {"start": v(18.6, -54.04) * mm, "mid": v(30.82, -48.13) * mm, "end": v(41.3, -39.5) * mm});
            skArc(sketch, "E36.0.3", {"start": v(41.3, -39.5) * mm, "mid": v(43.59, -38.76) * mm, "end": v(45.47, -40.25) * mm});
            skArc(sketch, "E36.0.4", {"start": v(45.47, -40.25) * mm, "mid": v(48.78, -59.31) * mm, "end": v(43.04, -77.79) * mm});
            skArc(sketch, "E36.0.5", {"start": v(43.04, -77.79) * mm, "mid": v(45.65, -76.28) * mm, "end": v(48.21, -74.7) * mm});
            skArc(sketch, "E36.0.6", {"start": v(48.21, -74.7) * mm, "mid": v(52, -54.9) * mm, "end": v(46.66, -35.45) * mm});
            skArc(sketch, "E36.0.7", {"start": v(46.66, -35.45) * mm, "mid": v(46.36, -34.1) * mm, "end": v(46.81, -32.78) * mm});
            skArc(sketch, "E36.0.8", {"start": v(46.81, -32.78) * mm, "mid": v(53.22, -20.82) * mm, "end": v(56.63, -7.68) * mm});
            skArc(sketch, "E36.0.9", {"start": v(56.63, -7.68) * mm, "mid": v(58.04, -5.74) * mm, "end": v(60.44, -5.83) * mm});
            skArc(sketch, "E36.0.10", {"start": v(60.44, -5.83) * mm, "mid": v(74.32, -19.31) * mm, "end": v(80.54, -37.63) * mm});
            skArc(sketch, "E36.0.11", {"start": v(80.54, -37.63) * mm, "mid": v(81.77, -34.88) * mm, "end": v(82.9, -32.09) * mm});
            skArc(sketch, "E36.0.12", {"start": v(82.9, -32.09) * mm, "mid": v(74.34, -13.84) * mm, "end": v(58.59, -1.25) * mm});
            skArc(sketch, "E36.0.13", {"start": v(58.59, -1.25) * mm, "mid": v(57.54, -0.33) * mm, "end": v(57.14, 1) * mm});
            skArc(sketch, "E36.0.14", {"start": v(57.14, 1) * mm, "mid": v(55.3, 14.44) * mm, "end": v(50.33, 27.07) * mm});
            skArc(sketch, "E36.0.15", {"start": v(50.33, 27.07) * mm, "mid": v(50.33, 29.48) * mm, "end": v(52.33, 30.8) * mm});
            skArc(sketch, "E36.0.16", {"start": v(52.33, 30.8) * mm, "mid": v(71.48, 28.06) * mm, "end": v(87.28, 16.9) * mm});
            skArc(sketch, "E36.0.17", {"start": v(87.28, 16.9) * mm, "mid": v(86.66, 19.84) * mm, "end": v(85.93, 22.77) * mm});
            skArc(sketch, "E36.0.18", {"start": v(85.93, 22.77) * mm, "mid": v(68.27, 32.5) * mm, "end": v(48.13, 33.42) * mm});
            skArc(sketch, "E36.0.19", {"start": v(48.13, 33.42) * mm, "mid": v(46.75, 33.55) * mm, "end": v(45.64, 34.4) * mm});
            skArc(sketch, "E36.0.20", {"start": v(45.64, 34.4) * mm, "mid": v(36.25, 44.19) * mm, "end": v(24.8, 51.49) * mm});
            skArc(sketch, "E36.0.21", {"start": v(24.8, 51.49) * mm, "mid": v(23.4, 53.43) * mm, "end": v(24.23, 55.68) * mm});
            skArc(sketch, "E36.0.22", {"start": v(24.23, 55.68) * mm, "mid": v(41.33, 64.72) * mm, "end": v(60.68, 64.97) * mm});
            skArc(sketch, "E36.0.23", {"start": v(60.68, 64.97) * mm, "mid": v(58.44, 66.99) * mm, "end": v(56.14, 68.93) * mm});
            skArc(sketch, "E36.0.24", {"start": v(56.14, 68.93) * mm, "mid": v(36.13, 66.42) * mm, "end": v(19.3, 55.33) * mm});
            skArc(sketch, "E36.0.25", {"start": v(19.3, 55.33) * mm, "mid": v(18.1, 54.62) * mm, "end": v(16.71, 54.65) * mm});
            skArc(sketch, "E36.0.26", {"start": v(16.71, 54.65) * mm, "mid": v(3.35, 57.05) * mm, "end": v(-10.2, 56.23) * mm});
            skArc(sketch, "E36.0.27", {"start": v(-10.2, 56.23) * mm, "mid": v(-12.48, 56.97) * mm, "end": v(-13.13, 59.29) * mm});
            skArc(sketch, "E36.0.28", {"start": v(-13.13, 59.29) * mm, "mid": v(-4.6, 76.65) * mm, "end": v(10.9, 88.23) * mm});
            skArc(sketch, "E36.0.29", {"start": v(10.9, 88.23) * mm, "mid": v(7.9, 88.55) * mm, "end": v(4.9, 88.76) * mm});
            skArc(sketch, "E36.0.30", {"start": v(4.9, 88.76) * mm, "mid": v(-9.8, 74.98) * mm, "end": v(-16.91, 56.1) * mm});
            skArc(sketch, "E36.0.31", {"start": v(-16.91, 56.1) * mm, "mid": v(-17.47, 54.83) * mm, "end": v(-18.6, 54.04) * mm});
            skArc(sketch, "E36.0.32", {"start": v(-18.6, 54.04) * mm, "mid": v(-30.82, 48.13) * mm, "end": v(-41.3, 39.5) * mm});
            skArc(sketch, "E36.0.33", {"start": v(-41.3, 39.5) * mm, "mid": v(-43.59, 38.76) * mm, "end": v(-45.47, 40.25) * mm});
            skArc(sketch, "E36.0.34", {"start": v(-45.47, 40.25) * mm, "mid": v(-48.78, 59.31) * mm, "end": v(-43.04, 77.79) * mm});
            skArc(sketch, "E36.0.35", {"start": v(-43.04, 77.79) * mm, "mid": v(-45.65, 76.28) * mm, "end": v(-48.21, 74.7) * mm});
            skArc(sketch, "E36.0.36", {"start": v(-48.21, 74.7) * mm, "mid": v(-52, 54.9) * mm, "end": v(-46.66, 35.45) * mm});
            skArc(sketch, "E36.0.37", {"start": v(-46.66, 35.45) * mm, "mid": v(-46.36, 34.1) * mm, "end": v(-46.81, 32.78) * mm});
            skArc(sketch, "E36.0.38", {"start": v(-46.81, 32.78) * mm, "mid": v(-53.22, 20.82) * mm, "end": v(-56.63, 7.68) * mm});
            skArc(sketch, "E36.0.39", {"start": v(-56.63, 7.68) * mm, "mid": v(-58.04, 5.74) * mm, "end": v(-60.44, 5.83) * mm});
            skArc(sketch, "E36.0.40", {"start": v(-60.44, 5.83) * mm, "mid": v(-74.32, 19.31) * mm, "end": v(-80.54, 37.63) * mm});
            skArc(sketch, "E36.0.41", {"start": v(-80.54, 37.63) * mm, "mid": v(-81.77, 34.88) * mm, "end": v(-82.9, 32.09) * mm});
            skArc(sketch, "E36.0.42", {"start": v(-82.9, 32.09) * mm, "mid": v(-74.34, 13.84) * mm, "end": v(-58.59, 1.25) * mm});
            skArc(sketch, "E36.0.43", {"start": v(-58.59, 1.25) * mm, "mid": v(-57.54, 0.33) * mm, "end": v(-57.14, -1) * mm});
            skArc(sketch, "E36.0.44", {"start": v(-57.14, -1) * mm, "mid": v(-55.3, -14.44) * mm, "end": v(-50.33, -27.07) * mm});
            skArc(sketch, "E36.0.45", {"start": v(-50.33, -27.07) * mm, "mid": v(-50.33, -29.48) * mm, "end": v(-52.33, -30.8) * mm});
            skArc(sketch, "E36.0.46", {"start": v(-52.33, -30.8) * mm, "mid": v(-71.48, -28.06) * mm, "end": v(-87.28, -16.9) * mm});
            skArc(sketch, "E36.0.47", {"start": v(-87.28, -16.9) * mm, "mid": v(-86.66, -19.84) * mm, "end": v(-85.93, -22.77) * mm});
            skArc(sketch, "E36.0.48", {"start": v(-85.93, -22.77) * mm, "mid": v(-68.27, -32.5) * mm, "end": v(-48.13, -33.42) * mm});
            skArc(sketch, "E36.0.49", {"start": v(-48.13, -33.42) * mm, "mid": v(-46.75, -33.55) * mm, "end": v(-45.64, -34.4) * mm});
            skArc(sketch, "E36.0.50", {"start": v(-45.64, -34.4) * mm, "mid": v(-36.25, -44.19) * mm, "end": v(-24.8, -51.49) * mm});
            skArc(sketch, "E36.0.51", {"start": v(-24.8, -51.49) * mm, "mid": v(-23.4, -53.43) * mm, "end": v(-24.23, -55.68) * mm});
            skArc(sketch, "E36.0.52", {"start": v(-24.23, -55.68) * mm, "mid": v(-41.33, -64.72) * mm, "end": v(-60.68, -64.97) * mm});
            skArc(sketch, "E36.0.53", {"start": v(-60.68, -64.97) * mm, "mid": v(-58.44, -66.99) * mm, "end": v(-56.14, -68.93) * mm});
            skArc(sketch, "E36.0.54", {"start": v(-56.14, -68.93) * mm, "mid": v(-36.13, -66.42) * mm, "end": v(-19.3, -55.33) * mm});
            skArc(sketch, "E36.0.55", {"start": v(-19.3, -55.33) * mm, "mid": v(-18.1, -54.62) * mm, "end": v(-16.71, -54.65) * mm});
            skArc(sketch, "E36.0.56", {"start": v(-16.71, -54.65) * mm, "mid": v(-3.35, -57.05) * mm, "end": v(10.2, -56.23) * mm});
            skArc(sketch, "E36.0.57", {"start": v(10.2, -56.23) * mm, "mid": v(12.48, -56.97) * mm, "end": v(13.13, -59.29) * mm});
            skArc(sketch, "E36.0.58", {"start": v(13.13, -59.29) * mm, "mid": v(4.6, -76.65) * mm, "end": v(-10.9, -88.23) * mm});
            skArc(sketch, "E36.0.59", {"start": v(-10.9, -88.23) * mm, "mid": v(-7.9, -88.55) * mm, "end": v(-4.9, -88.76) * mm});
            skCircle(sketch, "E37.0", {"center": v(0, 0) * mm, "radius": 53.98 * mm});
            skCircle(sketch, "E38.0", {"center": v(0, 0) * mm, "radius": 9.53 * mm});
            skCircle(sketch, "E39.0", {"center": v(0, 0) * mm, "radius": 3.81 * mm});
            skSolve(sketch);
        }
        {
            var Q0;
            Q0 = qSketchRegion(id + "F11", true);
            extrude(context, id + "F12", {"entities" : qUnion([Q0]), "operationType" : NewBodyOperationType.REMOVE, "endBound" : BoundingType.THROUGH_ALL, "depth" : 25.4 * mm, "hasSecondDirection" : true, "secondDirectionOppositeDirection" : true, "secondDirectionDepth" : 3.17 * mm});
        }
        {
            var Q0;
            {var subQ1=sQuery(id+"F0.wireOp",EDGE,"E0");var subQ2=makeQuery(id+"F1.opExtrude","SWEPT_FACE",FACE,{"disambiguationData":[OSD([subQ1])]});Q0=makeQuery(id+"F5.boolean.opBoolean","SPLIT",FACE,{"disambiguationData":[TD([makeQuery(id+"F5.opExtrude","SWEPT_FACE",FACE,{"disambiguationData":[OSD([sQuery(id+"F4.wireOp",EDGE,"E7.2.1")])]})])],"derivedFrom":makeQuery(id+"F3.boolean.opBoolean","SPLIT",FACE,{"disambiguationData":[TD([subQ2])],"derivedFrom":makeQuery(id+"F1.opExtrude","CAP_FACE",FACE,{"disambiguationData":[OSD([subQ1])],"isStart":false})})});}
            var sketch = newSketch(context, id + "F13", { "sketchPlane" : qUnion([Q0])});
            skCircle(sketch, "E40.0.0", {"center": v(0, 0) * mm, "radius": 9.53 * mm});
            skCircle(sketch, "E41.0", {"center": v(0, 0) * mm, "radius": 3.81 * mm});
            skSolve(sketch);
        }
        {
            var Q0;
            Q0 = qSketchRegion(id + "F13", true);
            extrude(context, id + "F14", {"entities" : qUnion([Q0]), "operationType" : NewBodyOperationType.REMOVE, "endBound" : BoundingType.THROUGH_ALL, "depth" : 25.4 * mm, "hasSecondDirection" : true, "secondDirectionOppositeDirection" : true, "secondDirectionDepth" : 3.17 * mm});
        }
        {
            var Q0;
            Q0=qCreatedBy(makeId("Front.planeOp"),FACE);
            cPlane(context, id + "F15", {"entities" : qUnion([Q0]), "cplaneType" : CPlaneType.OFFSET, "offset" : 25.4 * mm, "width" : 152.4 * mm, "height" : 152.4 * mm});
        }
        {
            var Q0;
            Q0=makeQuery(id+"F1.opExtrude","SWEPT_BODY",BODY,{"disambiguationData":[OSD([sQuery(id+"F0.wireOp",EDGE,"E0")])]});
            var Q1;
            Q1=qCreatedBy(id+"F15.planeOp",FACE);
            mirror(context, id + "F16", {"entities" : qUnion([Q0]), "mirrorPlane" : qUnion([Q1])});
        }
        {
            var Q0;
            Q0=makeQuery(id+"F1.opExtrude","SWEPT_BODY",BODY,{"disambiguationData":[OSD([sQuery(id+"F0.wireOp",EDGE,"E0")])]});
            deleteBodies(context, id + "F17", {"entities" : qUnion([Q0])});
        }
    });
